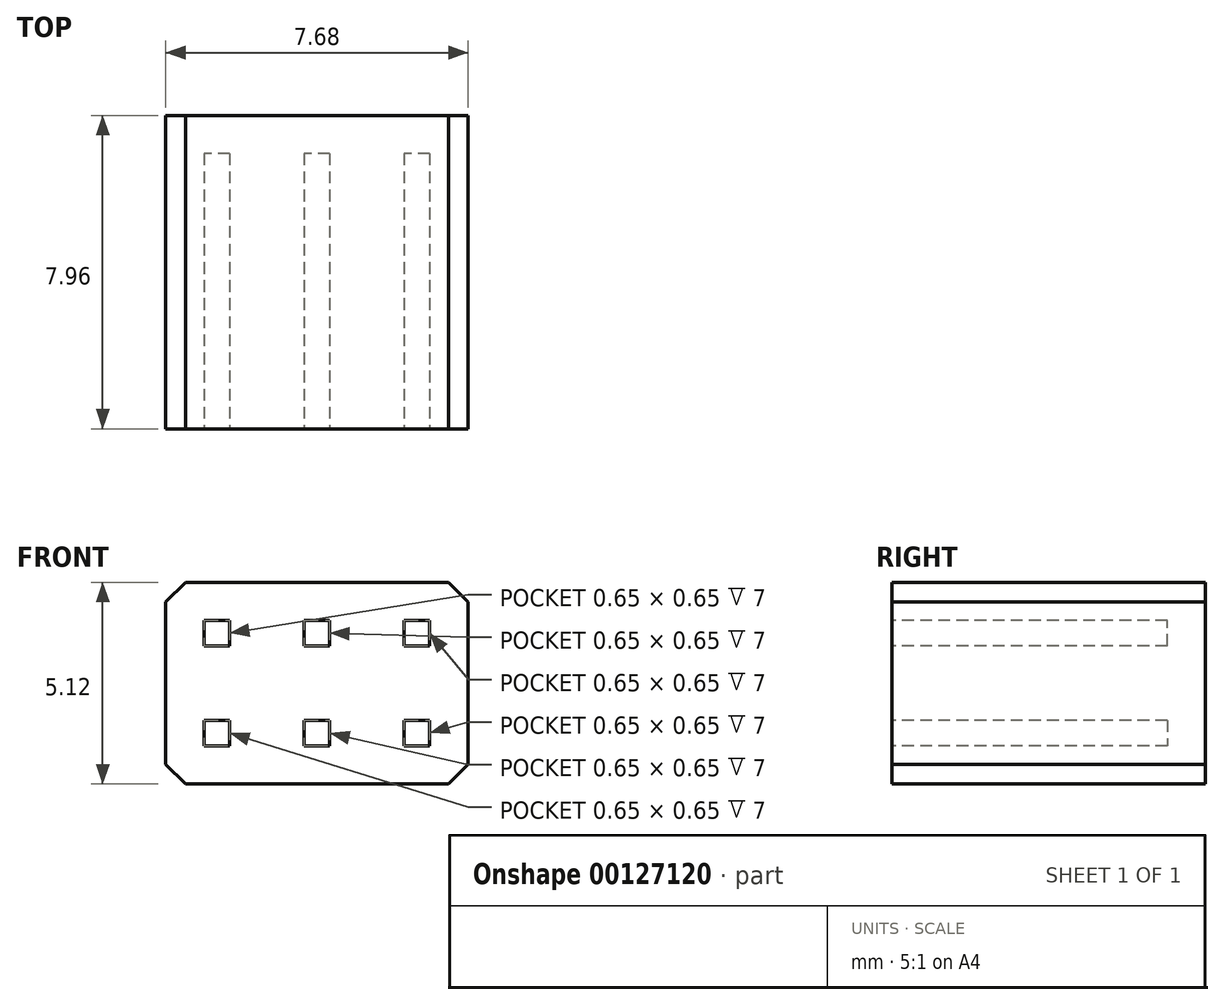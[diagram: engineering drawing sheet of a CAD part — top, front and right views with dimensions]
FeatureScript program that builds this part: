
annotation { "Feature Type Name" : "Feature", "Feature Type Description" : "" }
export const myFeature = defineFeature(function(context is Context, id is Id, definition is map)
    precondition{}
    {
        {
            var Q0;
            Q0=qCreatedBy(makeId("Front.planeOp"),FACE);
            var sketch = newSketch(context, id + "F0", { "sketchPlane" : qUnion([Q0])});
            skLineSegment(sketch, "E0.bottom", {"start": v(3.84, 2.56) * mm, "end": v(-3.84, 2.56) * mm});
            skLineSegment(sketch, "E0.top", {"start": v(3.84, -2.56) * mm, "end": v(-3.84, -2.56) * mm});
            skLineSegment(sketch, "E0.left", {"start": v(3.84, 2.56) * mm, "end": v(3.84, -2.56) * mm});
            skLineSegment(sketch, "E0.right", {"start": v(-3.84, 2.56) * mm, "end": v(-3.84, -2.56) * mm});
            skPoint(sketch, "E0.middle", {"position": v(0, 0) * mm});
            skLineSegment(sketch, "E1.bottom", {"start": v(-2.22, 0.94) * mm, "end": v(-2.87, 0.94) * mm});
            skLineSegment(sketch, "E1.top", {"start": v(-2.21, 1.6) * mm, "end": v(-2.87, 1.6) * mm});
            skLineSegment(sketch, "E1.left", {"start": v(-2.22, 0.94) * mm, "end": v(-2.22, 1.6) * mm});
            skLineSegment(sketch, "E1.right", {"start": v(-2.87, 0.94) * mm, "end": v(-2.87, 1.6) * mm});
            skPoint(sketch, "E1.middle", {"position": v(-2.54, 1.27) * mm});
            skLineSegment(sketch, "E2", {"start": v(-3.84, 0) * mm, "end": v(3.84, 0) * mm, "construction": true});
            skLineSegment(sketch, "E3.MirrorCS", {"start": v(-2.21, -0.95) * mm, "end": v(-2.87, -0.95) * mm});
            skLineSegment(sketch, "E4.MirrorCS", {"start": v(-2.87, -0.95) * mm, "end": v(-2.87, -1.6) * mm});
            skLineSegment(sketch, "E5.MirrorCS", {"start": v(-2.21, -1.6) * mm, "end": v(-2.86, -1.6) * mm});
            skLineSegment(sketch, "E6.MirrorCS", {"start": v(-2.21, -0.95) * mm, "end": v(-2.21, -1.6) * mm});
            skLineSegment(sketch, "E7.1.0.0", {"start": v(0.33, 0.95) * mm, "end": v(0.32, 1.6) * mm});
            skLineSegment(sketch, "E7.1.0.1", {"start": v(0.33, 1.6) * mm, "end": v(-0.33, 1.6) * mm});
            skLineSegment(sketch, "E7.1.0.2", {"start": v(-0.33, 0.95) * mm, "end": v(-0.33, 1.6) * mm});
            skLineSegment(sketch, "E7.1.0.3", {"start": v(0.32, 0.94) * mm, "end": v(-0.33, 0.94) * mm});
            skLineSegment(sketch, "E7.1.0.4", {"start": v(0.33, -0.95) * mm, "end": v(0.33, -1.6) * mm});
            skLineSegment(sketch, "E7.1.0.5", {"start": v(0.33, -0.95) * mm, "end": v(-0.33, -0.95) * mm});
            skLineSegment(sketch, "E7.1.0.6", {"start": v(-0.33, -0.95) * mm, "end": v(-0.32, -1.6) * mm});
            skLineSegment(sketch, "E7.1.0.7", {"start": v(0.33, -1.6) * mm, "end": v(-0.33, -1.6) * mm});
            skLineSegment(sketch, "E7.2.0.0", {"start": v(2.87, 0.94) * mm, "end": v(2.87, 1.6) * mm});
            skLineSegment(sketch, "E7.2.0.1", {"start": v(2.87, 1.6) * mm, "end": v(2.22, 1.6) * mm});
            skLineSegment(sketch, "E7.2.0.2", {"start": v(2.21, 0.94) * mm, "end": v(2.21, 1.6) * mm});
            skLineSegment(sketch, "E7.2.0.3", {"start": v(2.87, 0.95) * mm, "end": v(2.21, 0.95) * mm});
            skLineSegment(sketch, "E7.2.0.4", {"start": v(2.87, -0.94) * mm, "end": v(2.87, -1.6) * mm});
            skLineSegment(sketch, "E7.2.0.5", {"start": v(2.87, -0.95) * mm, "end": v(2.21, -0.95) * mm});
            skLineSegment(sketch, "E7.2.0.6", {"start": v(2.22, -0.94) * mm, "end": v(2.22, -1.6) * mm});
            skLineSegment(sketch, "E7.2.0.7", {"start": v(2.87, -1.6) * mm, "end": v(2.22, -1.6) * mm});
            skLineSegment(sketch, "E7.direction1", {"start": v(-2.21, -1.6) * mm, "end": v(0.33, -1.6) * mm, "construction": true});
            skLineSegment(sketch, "E8", {"start": v(0, 0) * mm, "end": v(0, -0.94) * mm, "construction": true});
            skSolve(sketch);
        }
        {
            var Q0;
            Q0=makeQuery(id+"F0.imprint","IMPRINT",FACE,{"disambiguationData":[TD([[makeQuery(id+"F0.imprint","IMPRINT",EDGE,{"derivedFrom":sQuery(id+"F0.wireOp",EDGE,"E0.bottom")}),1.0]])]});
            var Q1;
            Q1=makeQuery(id+"F0.imprint","IMPRINT",FACE,{"disambiguationData":[TD([[makeQuery(id+"F0.imprint","IMPRINT",EDGE,{"derivedFrom":sQuery(id+"F0.wireOp",EDGE,"E1.bottom")}),-1.0]])]});
            var Q2;
            Q2=makeQuery(id+"F0.imprint","IMPRINT",FACE,{"disambiguationData":[TD([[makeQuery(id+"F0.imprint","IMPRINT",EDGE,{"derivedFrom":sQuery(id+"F0.wireOp",EDGE,"E7.1.0.0")}),1.0]])]});
            var Q3;
            Q3=makeQuery(id+"F0.imprint","IMPRINT",FACE,{"disambiguationData":[TD([[makeQuery(id+"F0.imprint","IMPRINT",EDGE,{"derivedFrom":sQuery(id+"F0.wireOp",EDGE,"E7.2.0.0")}),1.0]])]});
            var Q4;
            Q4=makeQuery(id+"F0.imprint","IMPRINT",FACE,{"disambiguationData":[TD([[makeQuery(id+"F0.imprint","IMPRINT",EDGE,{"derivedFrom":sQuery(id+"F0.wireOp",EDGE,"E7.2.0.4")}),-1.0]])]});
            var Q5;
            Q5=makeQuery(id+"F0.imprint","IMPRINT",FACE,{"disambiguationData":[TD([[makeQuery(id+"F0.imprint","IMPRINT",EDGE,{"derivedFrom":sQuery(id+"F0.wireOp",EDGE,"E7.1.0.4")}),-1.0]])]});
            var Q6;
            Q6=makeQuery(id+"F0.imprint","IMPRINT",FACE,{"disambiguationData":[TD([[makeQuery(id+"F0.imprint","IMPRINT",EDGE,{"derivedFrom":sQuery(id+"F0.wireOp",EDGE,"E3.MirrorCS")}),1.0]])]});
            extrude(context, id + "F1", {"entities" : qUnion([Q0, Q1, Q2, Q3, Q4, Q5, Q6]), "oppositeDirection" : true, "depth" : 7.96 * mm});
        }
        {
            var Q0;
            Q0=makeQuery(id+"F0.imprint","IMPRINT",FACE,{"disambiguationData":[TD([[makeQuery(id+"F0.imprint","IMPRINT",EDGE,{"derivedFrom":sQuery(id+"F0.wireOp",EDGE,"E1.bottom")}),-1.0]])]});
            var Q1;
            Q1=makeQuery(id+"F0.imprint","IMPRINT",FACE,{"disambiguationData":[TD([[makeQuery(id+"F0.imprint","IMPRINT",EDGE,{"derivedFrom":sQuery(id+"F0.wireOp",EDGE,"E7.1.0.0")}),1.0]])]});
            var Q2;
            Q2=makeQuery(id+"F0.imprint","IMPRINT",FACE,{"disambiguationData":[TD([[makeQuery(id+"F0.imprint","IMPRINT",EDGE,{"derivedFrom":sQuery(id+"F0.wireOp",EDGE,"E7.2.0.0")}),1.0]])]});
            var Q3;
            Q3=makeQuery(id+"F0.imprint","IMPRINT",FACE,{"disambiguationData":[TD([[makeQuery(id+"F0.imprint","IMPRINT",EDGE,{"derivedFrom":sQuery(id+"F0.wireOp",EDGE,"E7.2.0.4")}),-1.0]])]});
            var Q4;
            Q4=makeQuery(id+"F0.imprint","IMPRINT",FACE,{"disambiguationData":[TD([[makeQuery(id+"F0.imprint","IMPRINT",EDGE,{"derivedFrom":sQuery(id+"F0.wireOp",EDGE,"E7.1.0.4")}),-1.0]])]});
            var Q5;
            Q5=makeQuery(id+"F0.imprint","IMPRINT",FACE,{"disambiguationData":[TD([[makeQuery(id+"F0.imprint","IMPRINT",EDGE,{"derivedFrom":sQuery(id+"F0.wireOp",EDGE,"E3.MirrorCS")}),1.0]])]});
            extrude(context, id + "F2", {"entities" : qUnion([Q0, Q1, Q2, Q3, Q4, Q5]), "operationType" : NewBodyOperationType.REMOVE, "oppositeDirection" : true, "depth" : 7 * mm});
        }
        {
            var Q0;
            Q0=makeQuery(id+"F1.opExtrude","SWEPT_EDGE",EDGE,{"disambiguationData":[OSD([sQuery(id+"F0.wireOp",EDGE,"E0.bottom"),sQuery(id+"F0.wireOp",EDGE,"E0.left")])]});
            var Q1;
            Q1=makeQuery(id+"F1.opExtrude","SWEPT_EDGE",EDGE,{"disambiguationData":[OSD([sQuery(id+"F0.wireOp",EDGE,"E0.bottom"),sQuery(id+"F0.wireOp",EDGE,"E0.right")])]});
            var Q2;
            Q2=makeQuery(id+"F1.opExtrude","SWEPT_EDGE",EDGE,{"disambiguationData":[OSD([sQuery(id+"F0.wireOp",EDGE,"E0.top"),sQuery(id+"F0.wireOp",EDGE,"E0.left")])]});
            var Q3;
            Q3=makeQuery(id+"F1.opExtrude","SWEPT_EDGE",EDGE,{"disambiguationData":[OSD([sQuery(id+"F0.wireOp",EDGE,"E0.top"),sQuery(id+"F0.wireOp",EDGE,"E0.right")])]});
            chamfer(context, id + "F3", {"entities" : qUnion([Q0, Q1, Q2, Q3]), "width" : 0.5 * mm, "tangentPropagation" : true});
        }
    });
